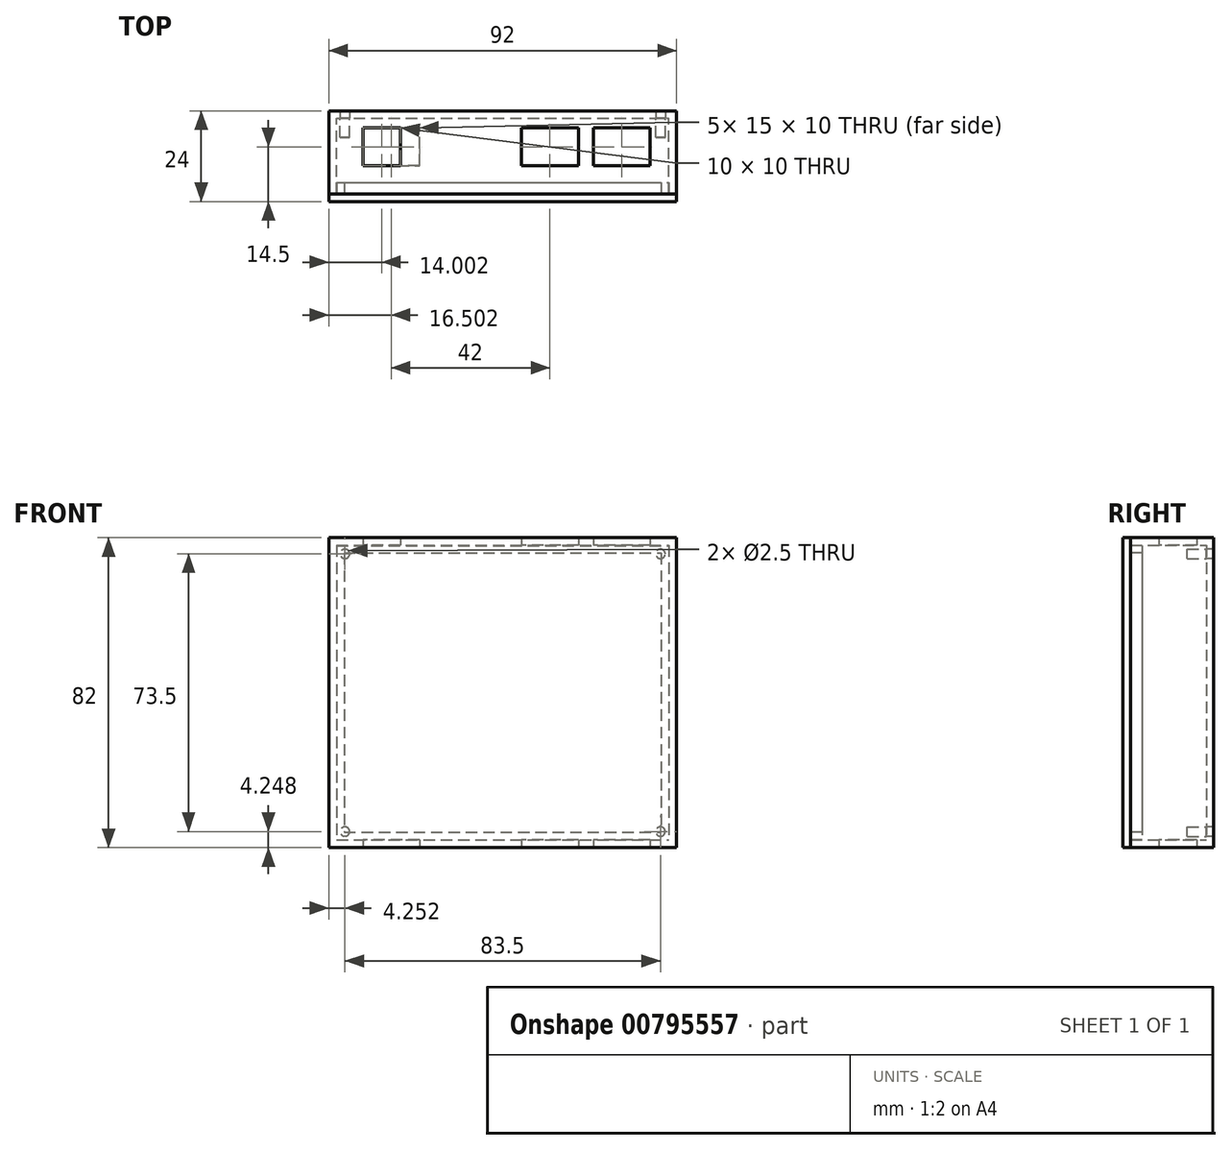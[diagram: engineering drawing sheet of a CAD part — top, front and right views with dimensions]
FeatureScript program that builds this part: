
annotation { "Feature Type Name" : "Feature", "Feature Type Description" : "" }
export const myFeature = defineFeature(function(context is Context, id is Id, definition is map)
    precondition{}
    {
        {
            var Q0;
            Q0=qCreatedBy(makeId("Front.planeOp"),FACE);
            var sketch = newSketch(context, id + "F0", { "sketchPlane" : qUnion([Q0])});
            skLineSegment(sketch, "E0.bottom", {"start": v(-54.96, 106.48) * mm, "end": v(37.04, 106.48) * mm});
            skLineSegment(sketch, "E0.top", {"start": v(-54.96, 24.48) * mm, "end": v(37.04, 24.48) * mm});
            skLineSegment(sketch, "E0.left", {"start": v(-54.96, 106.48) * mm, "end": v(-54.96, 24.48) * mm});
            skLineSegment(sketch, "E0.right", {"start": v(37.04, 106.48) * mm, "end": v(37.04, 24.48) * mm});
            skSolve(sketch);
        }
        {
            var Q0;
            Q0=makeQuery(id+"F0.imprint","IMPRINT",FACE,{"disambiguationData":[TD([[makeQuery(id+"F0.imprint","IMPRINT",EDGE,{"derivedFrom":sQuery(id+"F0.wireOp",EDGE,"E0.bottom")}),-1.0]])]});
            extrude(context, id + "F1", {"entities" : qUnion([Q0]), "oppositeDirection" : true, "depth" : 2 * mm, "offsetDistance" : 25 * mm});
        }
        {
            var Q0;
            Q0=makeQuery(id+"F1.opExtrude","CAP_FACE",FACE,{"disambiguationData":[OSD([sQuery(id+"F0.wireOp",EDGE,"E0.bottom"),sQuery(id+"F0.wireOp",EDGE,"E0.top"),sQuery(id+"F0.wireOp",EDGE,"E0.left"),sQuery(id+"F0.wireOp",EDGE,"E0.right")])],"isStart":true});
            var sketch = newSketch(context, id + "F2", { "sketchPlane" : qUnion([Q0])});
            skLineSegment(sketch, "E1.bottom", {"start": v(-52.96, 104.48) * mm, "end": v(35.04, 104.48) * mm});
            skLineSegment(sketch, "E1.top", {"start": v(-52.96, 26.48) * mm, "end": v(35.04, 26.48) * mm});
            skLineSegment(sketch, "E1.left", {"start": v(-52.96, 104.48) * mm, "end": v(-52.96, 26.48) * mm});
            skLineSegment(sketch, "E1.right", {"start": v(35.04, 104.48) * mm, "end": v(35.04, 26.48) * mm});
            skSolve(sketch);
        }
        {
            var Q0;
            Q0=makeQuery(id+"F2.imprint","IMPRINT",FACE,{"disambiguationData":[TD([[makeQuery(id+"F2.imprint","IMPRINT",EDGE,{"derivedFrom":sQuery(id+"F2.wireOp",EDGE,"E1.bottom")}),1.0]])]});
            extrude(context, id + "F3", {"entities" : qUnion([Q0]), "operationType" : NewBodyOperationType.ADD, "depth" : 20 * mm, "offsetDistance" : 25 * mm});
        }
        {
            var Q0;
            {var subQ0=sQuery(id+"F0.wireOp",EDGE,"E0.top");Q0=makeQuery(id+"F3.boolean.opBoolean","MERGE",FACE,{"derivedFrom":[makeQuery(id+"F1.opExtrude","SWEPT_FACE",FACE,{"disambiguationData":[OSD([subQ0])]}),makeQuery(id+"F3.opExtrude","SWEPT_FACE",FACE,{"disambiguationData":[OSD([subQ0])]})]});}
            var sketch = newSketch(context, id + "F4", { "sketchPlane" : qUnion([Q0])});
            skLineSegment(sketch, "E2.bottom", {"start": v(15.04, 12.5) * mm, "end": v(30.04, 12.5) * mm});
            skLineSegment(sketch, "E2.top", {"start": v(15.04, 2.5) * mm, "end": v(30.04, 2.5) * mm});
            skLineSegment(sketch, "E2.left", {"start": v(15.04, 12.5) * mm, "end": v(15.04, 2.5) * mm});
            skLineSegment(sketch, "E2.right", {"start": v(30.04, 12.5) * mm, "end": v(30.04, 2.5) * mm});
            skLineSegment(sketch, "E3.bottom", {"start": v(-3.96, 12.5) * mm, "end": v(11.04, 12.5) * mm});
            skLineSegment(sketch, "E3.top", {"start": v(-3.96, 2.5) * mm, "end": v(11.04, 2.5) * mm});
            skLineSegment(sketch, "E3.left", {"start": v(-3.96, 12.5) * mm, "end": v(-3.96, 2.5) * mm});
            skLineSegment(sketch, "E3.right", {"start": v(11.04, 12.5) * mm, "end": v(11.04, 2.5) * mm});
            skLineSegment(sketch, "E4.bottom", {"start": v(-45.96, 12.5) * mm, "end": v(-35.96, 12.5) * mm});
            skLineSegment(sketch, "E4.top", {"start": v(-45.96, 2.5) * mm, "end": v(-35.96, 2.5) * mm});
            skLineSegment(sketch, "E4.left", {"start": v(-45.96, 12.5) * mm, "end": v(-45.96, 2.5) * mm});
            skLineSegment(sketch, "E4.right", {"start": v(-35.96, 12.5) * mm, "end": v(-35.96, 2.5) * mm});
            skLineSegment(sketch, "E5.bottom", {"start": v(-35.96, 12.5) * mm, "end": v(-30.96, 12.5) * mm});
            skLineSegment(sketch, "E5.top", {"start": v(-35.96, 2.5) * mm, "end": v(-30.96, 2.5) * mm});
            skLineSegment(sketch, "E5.right", {"start": v(-30.96, 12.5) * mm, "end": v(-30.96, 2.5) * mm});
            skSolve(sketch);
        }
        {
            var Q0;
            Q0=makeQuery(id+"F4.imprint","IMPRINT",FACE,{"disambiguationData":[TD([[makeQuery(id+"F4.imprint","IMPRINT",EDGE,{"derivedFrom":sQuery(id+"F4.wireOp",EDGE,"E2.bottom")}),-1.0]])]});
            var Q1;
            Q1=makeQuery(id+"F4.imprint","IMPRINT",FACE,{"disambiguationData":[TD([[makeQuery(id+"F4.imprint","IMPRINT",EDGE,{"derivedFrom":sQuery(id+"F4.wireOp",EDGE,"E3.bottom")}),-1.0]])]});
            var Q2;
            Q2=makeQuery(id+"F4.imprint","IMPRINT",FACE,{"disambiguationData":[TD([[makeQuery(id+"F4.imprint","IMPRINT",EDGE,{"derivedFrom":sQuery(id+"F4.wireOp",EDGE,"E4.bottom")}),-1.0]])]});
            extrude(context, id + "F5", {"entities" : qUnion([Q0, Q1, Q2]), "operationType" : NewBodyOperationType.REMOVE, "oppositeDirection" : true, "depth" : 95 * mm, "offsetDistance" : 25 * mm});
        }
        {
            var Q0;
            Q0 = qSketchRegion(id + "F4", true);
            extrude(context, id + "F6", {"entities" : qUnion([Q0]), "operationType" : NewBodyOperationType.REMOVE, "oppositeDirection" : true, "depth" : 25 * mm, "offsetDistance" : 25 * mm});
        }
        {
            var Q0;
            Q0=makeQuery(id+"F1.opExtrude","CAP_FACE",FACE,{"disambiguationData":[OSD([sQuery(id+"F0.wireOp",EDGE,"E0.bottom"),sQuery(id+"F0.wireOp",EDGE,"E0.top"),sQuery(id+"F0.wireOp",EDGE,"E0.left"),sQuery(id+"F0.wireOp",EDGE,"E0.right")])],"isStart":true});
            var sketch = newSketch(context, id + "F7", { "sketchPlane" : qUnion([Q0])});
            skCircle(sketch, "E6", {"center": v(-50.7, 28.73) * mm, "radius": 1.25 * mm});
            skCircle(sketch, "E7.0.1.0", {"center": v(-50.7, 102.23) * mm, "radius": 1.25 * mm});
            skCircle(sketch, "E7.1.0.0", {"center": v(32.8, 28.73) * mm, "radius": 1.25 * mm});
            skCircle(sketch, "E7.1.1.0", {"center": v(32.8, 102.23) * mm, "radius": 1.25 * mm});
            skLineSegment(sketch, "E7.direction1", {"start": v(-50.7, 28.73) * mm, "end": v(32.8, 28.73) * mm, "construction": true});
            skLineSegment(sketch, "E7.direction2", {"start": v(-50.7, 28.73) * mm, "end": v(-50.7, 102.23) * mm, "construction": true});
            skSolve(sketch);
        }
        {
            var Q0;
            Q0=makeQuery(id+"F7.imprint","IMPRINT",FACE,{"disambiguationData":[TD([[makeQuery(id+"F7.imprint","IMPRINT",EDGE,{"derivedFrom":sQuery(id+"F7.wireOp",EDGE,"E6")}),1.0]])]});
            var Q1;
            Q1=makeQuery(id+"F7.imprint","IMPRINT",FACE,{"disambiguationData":[TD([[makeQuery(id+"F7.imprint","IMPRINT",EDGE,{"derivedFrom":sQuery(id+"F7.wireOp",EDGE,"E7.1.1.0")}),1.0]])]});
            extrude(context, id + "F8", {"entities" : qUnion([Q0, Q1]), "operationType" : NewBodyOperationType.ADD, "depth" : 5 * mm, "offsetDistance" : 25 * mm});
        }
        {
            var Q0;
            Q0=makeQuery(id+"F7.imprint","IMPRINT",FACE,{"disambiguationData":[TD([[makeQuery(id+"F7.imprint","IMPRINT",EDGE,{"derivedFrom":sQuery(id+"F7.wireOp",EDGE,"E7.1.0.0")}),1.0]])]});
            var Q1;
            Q1=makeQuery(id+"F7.imprint","IMPRINT",FACE,{"disambiguationData":[TD([[makeQuery(id+"F7.imprint","IMPRINT",EDGE,{"derivedFrom":sQuery(id+"F7.wireOp",EDGE,"E7.0.1.0")}),1.0]])]});
            extrude(context, id + "F9", {"entities" : qUnion([Q0, Q1]), "operationType" : NewBodyOperationType.REMOVE, "oppositeDirection" : true, "depth" : 25 * mm, "offsetDistance" : 25 * mm});
        }
        {
            var Q0;
            Q0=makeQuery(id+"F3.opExtrude","CAP_FACE",FACE,{"disambiguationData":[OSD([sQuery(id+"F0.wireOp",EDGE,"E0.bottom"),sQuery(id+"F0.wireOp",EDGE,"E0.top"),sQuery(id+"F0.wireOp",EDGE,"E0.left"),sQuery(id+"F0.wireOp",EDGE,"E0.right"),sQuery(id+"F2.wireOp",EDGE,"E1.bottom"),sQuery(id+"F2.wireOp",EDGE,"E1.top"),sQuery(id+"F2.wireOp",EDGE,"E1.left"),sQuery(id+"F2.wireOp",EDGE,"E1.right")])],"isStart":false});
            var sketch = newSketch(context, id + "F10", { "sketchPlane" : qUnion([Q0])});
            skLineSegment(sketch, "E8.bottom", {"start": v(-54.96, 106.48) * mm, "end": v(37.04, 106.48) * mm});
            skLineSegment(sketch, "E8.top", {"start": v(-54.96, 24.48) * mm, "end": v(37.04, 24.48) * mm});
            skLineSegment(sketch, "E8.left", {"start": v(-54.96, 106.48) * mm, "end": v(-54.96, 24.48) * mm});
            skLineSegment(sketch, "E8.right", {"start": v(37.04, 106.48) * mm, "end": v(37.04, 24.48) * mm});
            skSolve(sketch);
        }
        {
            var Q0;
            Q0 = qSketchRegion(id + "F10", true);
            extrude(context, id + "F11", {"entities" : qUnion([Q0]), "depth" : 2 * mm, "offsetDistance" : 25 * mm});
        }
        {
            var Q0;
            Q0=makeQuery(id+"F11.opExtrude","CAP_FACE",FACE,{"disambiguationData":[OSD([sQuery(id+"F10.wireOp",EDGE,"E8.bottom"),sQuery(id+"F10.wireOp",EDGE,"E8.top"),sQuery(id+"F10.wireOp",EDGE,"E8.left"),sQuery(id+"F10.wireOp",EDGE,"E8.right")])],"isStart":false});
            var sketch = newSketch(context, id + "F12", { "sketchPlane" : qUnion([Q0])});
            skLineSegment(sketch, "E9.bottom", {"start": v(-52.9, 104.43) * mm, "end": v(35, 104.43) * mm});
            skLineSegment(sketch, "E9.top", {"start": v(-52.9, 26.53) * mm, "end": v(35, 26.53) * mm});
            skLineSegment(sketch, "E9.left", {"start": v(-52.9, 104.43) * mm, "end": v(-52.9, 26.53) * mm});
            skLineSegment(sketch, "E9.right", {"start": v(35, 104.43) * mm, "end": v(35, 26.53) * mm});
            skLineSegment(sketch, "E10.bottom", {"start": v(-50.9, 102.43) * mm, "end": v(33, 102.43) * mm});
            skLineSegment(sketch, "E10.top", {"start": v(-50.9, 28.53) * mm, "end": v(33, 28.53) * mm});
            skLineSegment(sketch, "E10.left", {"start": v(-50.9, 102.43) * mm, "end": v(-50.9, 28.53) * mm});
            skLineSegment(sketch, "E10.right", {"start": v(33, 102.43) * mm, "end": v(33, 28.53) * mm});
            skSolve(sketch);
        }
        {
            var Q0;
            Q0=makeQuery(id+"F12.imprint","IMPRINT",FACE,{"disambiguationData":[TD([[makeQuery(id+"F12.imprint","IMPRINT",EDGE,{"derivedFrom":sQuery(id+"F12.wireOp",EDGE,"E9.bottom")}),-1.0]])]});
            extrude(context, id + "F13", {"entities" : qUnion([Q0]), "operationType" : NewBodyOperationType.ADD, "oppositeDirection" : true, "depth" : 5 * mm, "offsetDistance" : 25 * mm});
        }
    });
